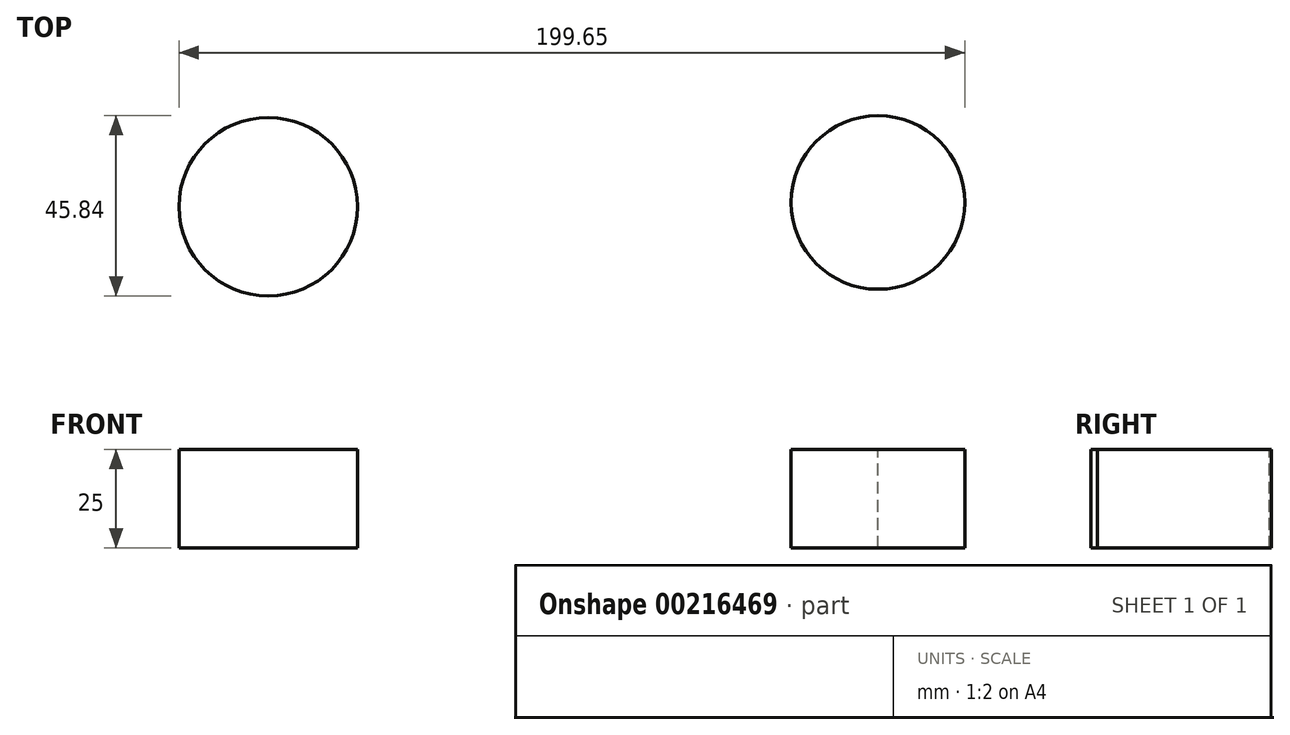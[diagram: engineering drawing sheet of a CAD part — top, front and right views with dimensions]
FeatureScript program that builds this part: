
annotation { "Feature Type Name" : "Feature", "Feature Type Description" : "" }
export const myFeature = defineFeature(function(context is Context, id is Id, definition is map)
    precondition{}
    {
        {
            var Q0;
            Q0=qCreatedBy(makeId("Top.planeOp"),FACE);
            var sketch = newSketch(context, id + "F0", { "sketchPlane" : qUnion([Q0])});
            skCircle(sketch, "E0", {"center": v(-98.58, 52.49) * mm, "radius": 22.68 * mm});
            skLineSegment(sketch, "E1.rect.bottom", {"start": v(-75.31, -40.57) * mm, "end": v(-120.68, -40.57) * mm});
            skLineSegment(sketch, "E1.rect.top", {"start": v(-75.31, -3.34) * mm, "end": v(-120.68, -3.34) * mm});
            skLineSegment(sketch, "E1.rect.left", {"start": v(-75.31, -40.57) * mm, "end": v(-75.31, -3.34) * mm});
            skLineSegment(sketch, "E1.rect.right", {"start": v(-120.68, -40.57) * mm, "end": v(-120.68, -3.34) * mm});
            skPoint(sketch, "E1.rect.middle", {"position": v(-98, -21.95) * mm});
            skLineSegment(sketch, "E2", {"start": v(32.28, -4.8) * mm, "end": v(32.28, -38.82) * mm});
            skLineSegment(sketch, "E3", {"start": v(32.28, -38.82) * mm, "end": v(84.62, -38.82) * mm});
            skLineSegment(sketch, "E4", {"start": v(84.62, -38.82) * mm, "end": v(84.62, -4.8) * mm});
            skLineSegment(sketch, "E5", {"start": v(84.62, -4.8) * mm, "end": v(32.28, -4.8) * mm});
            skArc(sketch, "E6", {"start": v(56.33, 75.65) * mm, "mid": v(56.33, 31.53) * mm, "end": v(56.33, 75.65) * mm});
            skSolve(sketch);
        }
        {
            var Q0;
            Q0=sQuery(id+"F0.wireOp",EDGE,"E6");
            var Q1;
            Q1=sQuery(id+"F0.wireOp",EDGE,"E0");
            extrude(context, id + "F1", {"bodyType" : ToolBodyType.SURFACE, "surfaceEntities" : qUnion([Q0, Q1]), "depth" : 25 * mm});
        }
    });
